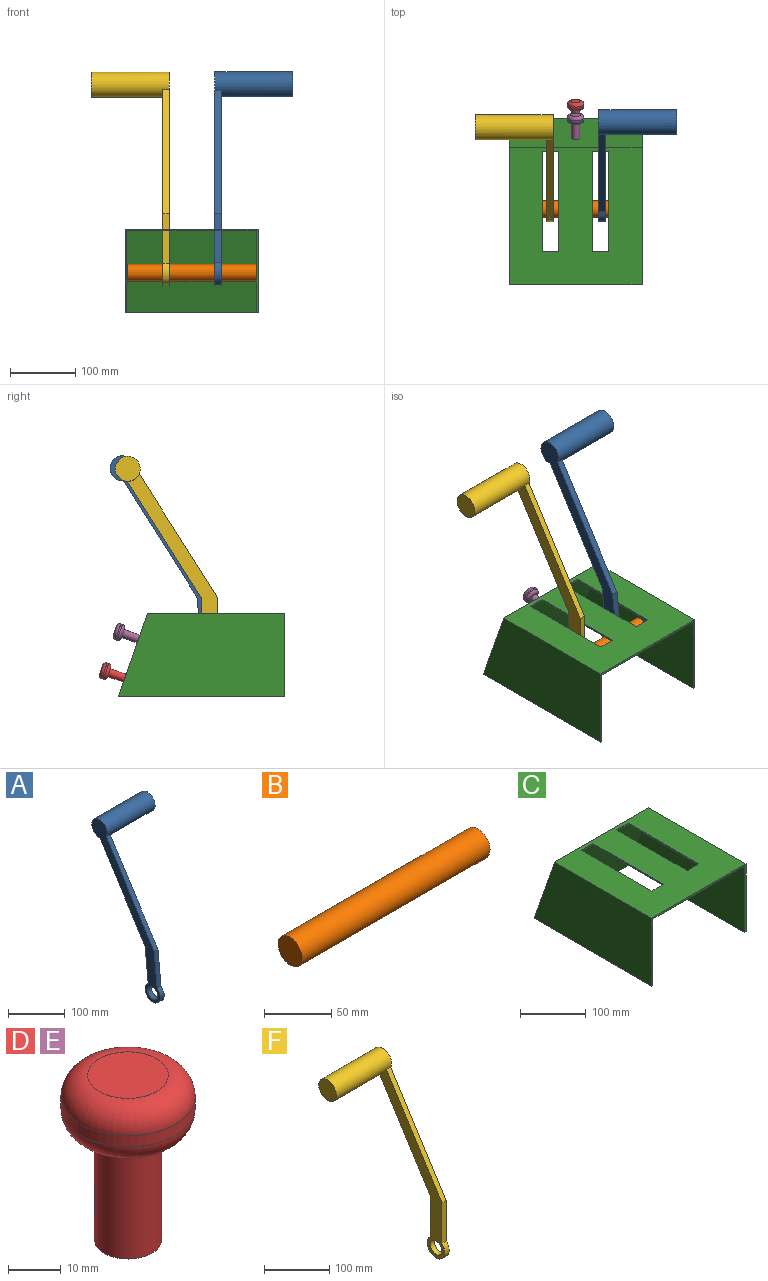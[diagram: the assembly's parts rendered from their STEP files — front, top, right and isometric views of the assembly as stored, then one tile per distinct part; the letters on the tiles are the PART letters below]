
ASSEMBLY  parts=6 mates=5
PART A: 10 faces, bbox 119.1x170.4x326 mm
  f0: plane 75.81x9.53mm, normal (0,-0.99,0.1), area 725.8mm2, adj f1,f5,f6,f7
  f1: cylinder r=19.05mm len=38.1mm, axis (-1,0,0), area 911.9mm2, adj f0,f2,f6,f7
  f2: plane 75.81x9.53mm, normal (0,0.99,-0.1), area 725.8mm2, adj f1,f3,f6,f7
  f3: plane 177.69x112.54mm, normal (0,0.84,-0.54), area 2003.4mm2, adj f2,f6,f7,f8
  f4: cylinder r=12.7mm len=25.4mm, axis (-1,0,0), area 760.1mm2, adj f6,f7
  f5: plane 187.82x118.95mm, normal (0,-0.84,0.54), area 2117.6mm2, adj f0,f6,f7,f8
  f6: plane 298.09x150.48mm, normal (1,0,0), area 6339.2mm2, adj f0,f1,f2,f3,f4,f5,f8
  f7: plane 326.04x170.38mm, normal (-1,0,0), area 7479.3mm2, adj f0,f1,f2,f3,f4,f5,f8
  f8: cylinder r=19.05mm len=119.06mm, axis (-1,0,0), area 14062.5mm2, adj f3,f5,f6,f7,f9
  f9: plane 38.1x38.1mm, normal (1,0,0), area 1140.1mm2, adj f8
PART B: 3 faces, bbox 196.9x25.4x25.4 mm
  f0: cylinder r=12.7mm len=196.85mm, axis (-1,0,0), area 15707.9mm2, adj f1,f2
  f1: plane 25.4x25.4mm, normal (1,0,0), area 506.7mm2, adj f0
  f2: plane 25.4x25.4mm, normal (-1,0,0), area 506.7mm2, adj f0
PART C: 18 faces, bbox 203.2x254x127 mm
  f0: plane 254x203.2mm, normal (0,0,-1), area 1823.5mm2, adj f1,f2,f11,f13,f14,f15,f17
  f1: plane 203.2x127mm, normal (0,-1,0), area 1148.4mm2, adj f0,f2,f11,f12,f14,f15,f16
  f2: plane 254x127mm, normal (1,0,0), area 29435.4mm2, adj f0,f1,f12,f13
  f3: plane 25.4x2.54mm, normal (0,-1,0), area 64.5mm2, adj f4,f9,f12,f16
  f4: plane 152.4x2.54mm, normal (-1,0,0), area 387.1mm2, adj f3,f5,f12,f16
  f5: plane 25.4x2.54mm, normal (0,1,0), area 64.5mm2, adj f4,f9,f12,f16
  f6: plane 25.4x2.54mm, normal (0,-1,0), area 64.5mm2, adj f7,f10,f12,f16
  f7: plane 152.4x2.54mm, normal (-1,0,0), area 387.1mm2, adj f6,f8,f12,f16
  f8: plane 25.4x2.54mm, normal (0,1,0), area 64.5mm2, adj f7,f10,f12,f16
  f9: plane 152.4x2.54mm, normal (1,0,0), area 387.1mm2, adj f3,f5,f12,f16
  f10: plane 152.4x2.54mm, normal (1,0,0), area 387.1mm2, adj f6,f8,f12,f16
  f11: plane 254x127mm, normal (-1,0,0), area 29435.4mm2, adj f0,f1,f12,f13
  f12: plane 209.55x203.2mm, normal (0,0,1), area 34838.6mm2, adj f1,f2,f3,f4,f5,f6,f7,f8
  f13: plane 203.2x127mm, normal (0,0.94,0.33), area 27341.4mm2, adj f0,f2,f11,f12
  f14: plane 251.31x124.46mm, normal (-1,0,0), area 28567.1mm2, adj f0,f1,f16,f17
  f15: plane 251.31x124.46mm, normal (1,0,0), area 28567.1mm2, adj f0,f1,f16,f17
  f16: plane 207.75x198.12mm, normal (0,0,-1), area 33417.1mm2, adj f1,f3,f4,f5,f6,f7,f8,f9
  f17: plane 198.12x124.46mm, normal (0,-0.94,-0.33), area 26124.7mm2, adj f0,f14,f15,f16
PART D: 7 faces, bbox 27.5x27.5x38.1 mm
  f0: cylinder r=6.35mm len=25.4mm, axis (0,0,1), area 1013.4mm2, adj f1,f3
  f1: plane 12.7x12.7mm, normal (0,0,-1), area 126.7mm2, adj f0
  f2: cylinder r=12.7mm len=25.4mm, axis (0,0,-1), area 202.7mm2, adj f5,f6
  f3: plane 15.24x15.24mm, normal (0,0,-1), area 55.7mm2, adj f0,f5
  f4: plane 15.24x15.24mm, normal (0,0,1), area 182.4mm2, adj f6
  f5: torus R=7.62mm, axis (0,0,1), area 544.2mm2, adj f2,f3
  f6: torus R=7.62mm, axis (0,0,1), area 544.2mm2, adj f2,f4
PART E: same geometry as D
PART F: 10 faces, bbox 119.1x162.7x325.2 mm
  f0: plane 76.2x9.53mm, normal (0,-1,0), area 725.8mm2, adj f1,f5,f6,f7
  f1: cylinder r=19.05mm len=38.1mm, axis (-1,0,0), area 875.3mm2, adj f0,f2,f6,f7
  f2: plane 76.2x9.53mm, normal (0,1,0), area 725.8mm2, adj f1,f3,f6,f7
  f3: plane 177.69x112.54mm, normal (0,0.84,-0.54), area 2003.3mm2, adj f2,f6,f7,f8
  f4: cylinder r=12.7mm len=25.4mm, axis (-1,0,0), area 760.1mm2, adj f6,f7
  f5: plane 189.17x119.81mm, normal (0,-0.84,0.54), area 2132.8mm2, adj f0,f6,f7,f8
  f6: plane 325.22x162.69mm, normal (1,0,0), area 8235.3mm2, adj f0,f1,f2,f3,f4,f5,f8
  f7: plane 298.62x144.29mm, normal (-1,0,0), area 7095.2mm2, adj f0,f1,f2,f3,f4,f5,f8
  f8: cylinder r=19.05mm len=119.06mm, axis (-1,0,0), area 14034mm2, adj f3,f5,f6,f7,f9
  f9: plane 38.1x38.1mm, normal (-1,0,0), area 1140.1mm2, adj f8
PLACE A t=(130.21,72.14,-125.78)mm
PLACE B t=(90.52,68.3,-179.1)mm
PLACE C t=(89.88,80.19,-239.36)mm
PLACE D rot(axis=(-1,0,0),70.7deg) t=(89.88,221.53,-203.43)mm
PLACE E rot(axis=(-1,0,0),70.7deg) t=(89.88,200.55,-143.49)mm
PLACE F t=(50.83,112.84,52.46)mm
MATE fastened E.f0 <-> C.f13  axis (0,-0.94,-0.33) through (89.88,176.58,-151.88)mm
MATE fastened D.f0 <-> C.f13  axis (0,-0.94,-0.33) through (89.88,197.55,-211.82)mm
MATE revolute A.f1 <-> B.f0  axis (-1,0,0) through (125.44,68.3,-179.1)mm
MATE revolute F.f1 <-> B.f0  axis (-1,0,0) through (55.59,68.3,-179.1)mm
MATE fastened C.f14 <-> B.f0  axis (-1,0,0) through (188.94,68.3,-179.1)mm
